# Revit family: HSS-Round Hollow Structural Section-Column
name_source: partatom
category: Structural Columns
revit_build: Autodesk Revit Architecture 2012 (Build: 20110210_1515)
units: mm (PartAtom-declared; Revit-internal decimal feet)

## types (153) — shared parameters
Assembly Code = B10

## per-type parameters (varying)
| type | A | OD | W | t |
| HSS20X0.500 | 28.5 in² | 1' - 8" | 104 | 0' - 0 15/32" |
| HSS20X0.375 | 21.5 in² | 1' - 8" | 78.7 | 0' - 0 11/32" |
| HSS18X0.500 | 25.6 in² | 1' - 6" | 93.5 | 0' - 0 15/32" |
| HSS18X0.375 | 19.4 in² | 1' - 6" | 70.7 | 0' - 0 11/32" |
| HSS16X0.625 | 28.1 in² | 1' - 4" | 103 | 0' - 0 19/32" |
| HSS16X0.500 | 22.7 in² | 1' - 4" | 82.8 | 0' - 0 15/32" |
| HSS16X0.438 | 19.9 in² | 1' - 4" | 72.9 | 0' - 0 13/32" |
| HSS16X0.375 | 17.2 in² | 1' - 4" | 62.6 | 0' - 0 11/32" |
| HSS16X0.312 | 14.4 in² | 1' - 4" | 52.3 | 0' - 0 9/32" |
| HSS16X0.250 | 11.5 in² | 1' - 4" | 42.1 | 0' - 0 7/32" |
| HSS14X0.625 | 24.5 in² | 1' - 2" | 89.4 | 0' - 0 19/32" |
| HSS14X0.500 | 19.8 in² | 1' - 2" | 72.2 | 0' - 0 15/32" |
| HSS14X0.375 | 15 in² | 1' - 2" | 54.6 | 0' - 0 11/32" |
| HSS14X0.312 | 12.5 in² | 1' - 2" | 45.7 | 0' - 0 9/32" |
| HSS14X0.250 | 10.1 in² | 1' - 2" | 36.7 | 0' - 0 7/32" |
| HSS12.750X0.500 | 17.9 in² | 1' - 0 3/4" | 65.5 | 0' - 0 15/32" |
| HSS12.750X0.375 | 13.6 in² | 1' - 0 3/4" | 49.6 | 0' - 0 11/32" |
| HSS12.750X0.250 | 9.16 in² | 1' - 0 3/4" | 33.4 | 0' - 0 7/32" |
| HSS12.500X.625 - Obsolete | 21.8 in² | 1' - 0 1/2" | 79.3 | 0' - 0 19/32" |
| HSS12.500X.500 - Obsolete | 17.6 in² | 1' - 0 1/2" | 64.1 | 0' - 0 15/32" |
| HSS12.500X.375 - Obsolete | 13.3 in² | 1' - 0 1/2" | 48.6 | 0' - 0 11/32" |
| HSS12.500X.312 - Obsolete | 11.2 in² | 1' - 0 1/2" | 40.7 | 0' - 0 9/32" |
| HSS12.500X.250 - Obsolete | 9 in² | 1' - 0 1/2" | 32.7 | 0' - 0 7/32" |
| HSS12.500X.188 - Obsolete | 6.7 in² | 1' - 0 1/2" | 24.7 | 0' - 0 3/16" |
| HSS11.250X.625 - Obsolete | 19.5 in² | 0' - 11 1/4" | 71 | 0' - 0 19/32" |
| HSS11.250X.500 - Obsolete | 15.8 in² | 0' - 11 1/4" | 57.5 | 0' - 0 15/32" |
| HSS11.250X.375 - Obsolete | 12 in² | 0' - 11 1/4" | 43.6 | 0' - 0 11/32" |
| HSS11.250X.312 - Obsolete | 10 in² | 0' - 11 1/4" | 36.5 | 0' - 0 9/32" |
| HSS11.250X.250 - Obsolete | 8.1 in² | 0' - 11 1/4" | 29.4 | 0' - 0 7/32" |
| HSS11.250X.188 - Obsolete | 6.1 in² | 0' - 11 1/4" | 22.2 | 0' - 0 3/16" |
| HSS10.750X0.500 | 15 in² | 0' - 10 3/4" | 54.8 | 0' - 0 15/32" |
| HSS10.750X0.375 | 11.4 in² | 0' - 10 3/4" | 41.6 | 0' - 0 11/32" |
| HSS10.750X0.250 | 7.7 in² | 0' - 10 3/4" | 28.1 | 0' - 0 7/32" |
| HSS10X0.625 | 17.2 in² | 0' - 10" | 62.6 | 0' - 0 19/32" |
| HSS10X0.500 | 13.9 in² | 0' - 10" | 50.8 | 0' - 0 15/32" |
| HSS10X0.375 | 10.6 in² | 0' - 10" | 38.6 | 0' - 0 11/32" |
| HSS10X0.312 | 8.88 in² | 0' - 10" | 32.3 | 0' - 0 9/32" |
| HSS10X0.250 | 7.15 in² | 0' - 10" | 26.1 | 0' - 0 7/32" |
| HSS10X0.188 | 5.37 in² | 0' - 10" | 19.7 | 0' - 0 3/16" |
| HSS9.625X0.500 | 13.4 in² | 0' - 9 5/8" | 48.8 | 0' - 0 15/32" |
| HSS9.625X0.375 | 10.2 in² | 0' - 9 5/8" | 37.1 | 0' - 0 11/32" |
| HSS9.625X0.312 | 8.53 in² | 0' - 9 5/8" | 31.1 | 0' - 0 9/32" |
| HSS9.625X0.250 | 6.87 in² | 0' - 9 5/8" | 25.1 | 0' - 0 7/32" |
| HSS9.625X0.188 | 5.17 in² | 0' - 9 5/8" | 19 | 0' - 0 3/16" |
| HSS8.750X.500 - Obsolete | 12.1 in² | 0' - 8 3/4" | 44.1 | 0' - 0 15/32" |
| HSS8.750X.375 - Obsolete | 9.2 in² | 0' - 8 3/4" | 33.6 | 0' - 0 11/32" |
| HSS8.750X.312 - Obsolete | 7.7 in² | 0' - 8 3/4" | 28.1 | 0' - 0 9/32" |
| HSS8.750X.250 - Obsolete | 6.2 in² | 0' - 8 3/4" | 22.7 | 0' - 0 7/32" |
| HSS8.750X.188 - Obsolete | 4.7 in² | 0' - 8 3/4" | 17.2 | 0' - 0 3/16" |
| HSS8.625X0.625 | 14.7 in² | 0' - 8 5/8" | 53.5 | 0' - 0 19/32" |
| HSS8.625X0.500 | 11.9 in² | 0' - 8 5/8" | 43.4 | 0' - 0 15/32" |
| HSS8.625X0.375 | 9.07 in² | 0' - 8 5/8" | 33.1 | 0' - 0 11/32" |
| HSS8.625X0.322 | 7.85 in² | 0' - 8 5/8" | 28.6 | 0' - 0 5/16" |
| HSS8.625X0.250 | 6.14 in² | 0' - 8 5/8" | 22.4 | 0' - 0 7/32" |
| HSS8.625X0.188 | 4.62 in² | 0' - 8 5/8" | 17 | 0' - 0 3/16" |
| HSS7.625X0.375 | 7.98 in² | 0' - 8 5/8" | 29.1 | 0' - 0 11/32" |
| HSS7.625X0.328 | 7.01 in² | 0' - 8 5/8" | 25.6 | 0' - 0 5/16" |
| HSS7.625X0.125 - Obsolete | 2.7 in² | 0' - 7 5/8" | 10 | 0' - 0 1/8" |
| HSS7.500X0.500 | 10.3 in² | 0' - 7 1/2" | 37.4 | 0' - 0 15/32" |
| HSS7.500X0.375 | 7.84 in² | 0' - 7 1/2" | 28.6 | 0' - 0 11/32" |
| HSS7.500X0.312 | 6.59 in² | 0' - 7 1/2" | 24 | 0' - 0 9/32" |
| HSS7.500X0.250 | 5.32 in² | 0' - 7 1/2" | 19.4 | 0' - 0 7/32" |
| HSS7.500X0.188 | 4 in² | 0' - 7 1/2" | 14.7 | 0' - 0 3/16" |
| HSS7X0.500 | 9.55 in² | 0' - 7" | 34.7 | 0' - 0 15/32" |
| HSS7X0.375 | 7.29 in² | 0' - 7" | 26.6 | 0' - 0 11/32" |
| HSS7X0.312 | 6.13 in² | 0' - 7" | 22.3 | 0' - 0 9/32" |
| HSS7X0.250 | 4.95 in² | 0' - 7" | 18 | 0' - 0 7/32" |
| HSS7X0.188 | 3.73 in² | 0' - 7" | 13.7 | 0' - 0 3/16" |
| HSS7X0.125 | 2.51 in² | 0' - 7" | 9.19 | 0' - 0 1/8" |
| HSS6.875X0.500 | 9.36 in² | 0' - 6 7/8" | 34.1 | 0' - 0 15/32" |
| HSS6.875X0.375 | 7.16 in² | 0' - 6 7/8" | 26.1 | 0' - 0 11/32" |
| HSS6.875X0.312 | 6.02 in² | 0' - 6 7/8" | 21.9 | 0' - 0 9/32" |
| HSS6.875X0.250 | 4.86 in² | 0' - 6 7/8" | 17.7 | 0' - 0 7/32" |
| HSS6.875X0.188 | 3.66 in² | 0' - 6 7/8" | 13.4 | 0' - 0 3/16" |
| HSS6.625X0.500 | 9 in² | 0' - 6 5/8" | 32.7 | 0' - 0 15/32" |
| HSS6.625X0.432 | 7.86 in² | 0' - 6 5/8" | 28.6 | 0' - 0 13/32" |
| HSS6.625X0.375 | 6.88 in² | 0' - 6 5/8" | 25.1 | 0' - 0 11/32" |
| HSS6.625X0.312 | 5.79 in² | 0' - 6 5/8" | 21.1 | 0' - 0 9/32" |
| HSS6.625X0.280 | 5.2 in² | 0' - 6 5/8" | 19 | 0' - 0 1/4" |
| HSS6.625X0.250 | 4.68 in² | 0' - 6 5/8" | 17 | 0' - 0 7/32" |
| HSS6.625X0.188 | 3.53 in² | 0' - 6 5/8" | 12.9 | 0' - 0 3/16" |
| HSS6.625X0.125 | 2.37 in² | 0' - 6 5/8" | 8.69 | 0' - 0 1/8" |
| HSS6.125X0.500 - Obsolete | 8.3 in² | 0' - 6 1/8" | 30.1 | 0' - 0 15/32" |
| HSS6.125X0.375 - Obsolete | 6.3 in² | 0' - 6 1/8" | 23.1 | 0' - 0 11/32" |
| HSS6.125X0.312 - Obsolete | 5.3 in² | 0' - 6 1/8" | 19.4 | 0' - 0 9/32" |
| HSS6.125X0.250 - Obsolete | 4.3 in² | 0' - 6 1/8" | 15.7 | 0' - 0 7/32" |
| HSS6.125X0.188 - Obsolete | 3.3 in² | 0' - 6 1/8" | 11.9 | 0' - 0 3/16" |
| HSS6X0.500 | 8.09 in² | 0' - 6" | 29.4 | 0' - 0 15/32" |
| HSS6X0.375 | 6.2 in² | 0' - 6" | 22.5 | 0' - 0 11/32" |
| HSS6X0.312 | 5.22 in² | 0' - 6" | 19 | 0' - 0 9/32" |
| HSS6X0.280 | 4.69 in² | 0' - 6" | 17.1 | 0' - 0 1/4" |
| HSS6X0.250 | 4.22 in² | 0' - 6" | 15.4 | 0' - 0 7/32" |
| HSS6X0.188 | 3.18 in² | 0' - 6" | 11.7 | 0' - 0 3/16" |
| HSS6X0.125 | 2.14 in² | 0' - 6" | 7.85 | 0' - 0 1/8" |
| HSS5.563X0.500 | 7.45 in² | 0' - 5 9/16" | 27.1 | 0' - 0 15/32" |
| HSS5.563X0.375 | 5.72 in² | 0' - 5 9/16" | 20.8 | 0' - 0 11/32" |
| HSS5.563X0.258 | 4.01 in² | 0' - 5 9/16" | 14.6 | 0' - 0 1/4" |
| HSS5.563X0.188 | 2.95 in² | 0' - 5 9/16" | 10.8 | 0' - 0 3/16" |
| HSS5.563X0.134 | 2.12 in² | 0' - 5 9/16" | 7.78 | 0' - 0 1/8" |
| HSS5.500X0.500 | 7.36 in² | 0' - 5 1/2" | 26.7 | 0' - 0 15/32" |
| HSS5.500X0.375 | 5.65 in² | 0' - 5 1/2" | 20.5 | 0' - 0 11/32" |
| HSS5.500X0.258 | 3.97 in² | 0' - 5 1/2" | 14.5 | 0' - 0 1/4" |
| HSS5X0.500 | 6.62 in² | 0' - 5" | 24.1 | 0' - 0 15/32" |
| HSS5X0.375 | 5.1 in² | 0' - 5" | 18.5 | 0' - 0 11/32" |
| HSS5X0.312 | 4.3 in² | 0' - 5" | 15.6 | 0' - 0 9/32" |
| HSS5X0.258 | 3.59 in² | 0' - 5" | 13.1 | 0' - 0 1/4" |
| HSS5X0.250 | 3.49 in² | 0' - 5" | 12.7 | 0' - 0 7/32" |
| HSS5X0.188 | 2.64 in² | 0' - 5" | 9.67 | 0' - 0 3/16" |
| HSS5X0.125 | 1.78 in² | 0' - 5" | 6.51 | 0' - 0 1/8" |
| HSS4.500X0.375 | 4.55 in² | 0' - 4 1/2" | 16.5 | 0' - 0 11/32" |
| HSS4.500X0.337 | 4.12 in² | 0' - 4 1/2" | 15 | 0' - 0 5/16" |
| HSS4.500X0.237 | 2.96 in² | 0' - 4 1/2" | 10.8 | 0' - 0 7/32" |
| HSS4.500X0.188 | 2.36 in² | 0' - 4 1/2" | 8.67 | 0' - 0 3/16" |
| HSS4.500X0.125 | 1.6 in² | 0' - 4 1/2" | 5.85 | 0' - 0 1/8" |
| HSS4X0.337 - Obsolete | 3.7 in² | 0' - 4" | 13.2 | 0' - 0 5/16" |
| HSS4X0.313 | 3.39 in² | 0' - 4" | 12.3 | 0' - 0 9/32" |
| HSS4X0.250 | 2.76 in² | 0' - 4" | 10 | 0' - 0 7/32" |
| HSS4X0.237 | 2.61 in² | 0' - 4" | 9.53 | 0' - 0 7/32" |
| HSS4X0.226 | 2.5 in² | 0' - 4" | 9.12 | 0' - 0 7/32" |
| HSS4X0.220 | 2.44 in² | 0' - 4" | 8.89 | 0' - 0 7/32" |
| HSS4X0.188 | 2.09 in² | 0' - 4" | 7.66 | 0' - 0 3/16" |
| HSS4X0.125 | 1.42 in² | 0' - 4" | 5.18 | 0' - 0 1/8" |
| HSS3.500X0.313 | 2.93 in² | 0' - 3 1/2" | 10.7 | 0' - 0 9/32" |
| HSS3.500X0.300 | 2.82 in² | 0' - 3 1/2" | 10.3 | 0' - 0 9/32" |
| HSS3.500X0.250 | 2.39 in² | 0' - 3 1/2" | 8.69 | 0' - 0 7/32" |
| HSS3.500X0.216 | 2.08 in² | 0' - 3 1/2" | 7.58 | 0' - 0 3/16" |
| HSS3.500X0.203 | 1.97 in² | 0' - 3 1/2" | 7.15 | 0' - 0 3/16" |
| HSS3.500X0.188 | 1.82 in² | 0' - 3 1/2" | 6.66 | 0' - 0 3/16" |
| HSS3.500X0.125 | 1.23 in² | 0' - 3 1/2" | 4.51 | 0' - 0 1/8" |
| HSS3X0.300 - Obsolete | 2.4 in² | 0' - 3" | 8.7 | 0' - 0 9/32" |
| HSS3X0.250 | 2.03 in² | 0' - 3" | 7.35 | 0' - 0 7/32" |
| HSS3X0.216 | 1.77 in² | 0' - 3" | 6.43 | 0' - 0 3/16" |
| HSS3X0.203 | 1.67 in² | 0' - 3" | 6.07 | 0' - 0 3/16" |
| HSS3X0.188 | 1.54 in² | 0' - 3" | 5.65 | 0' - 0 3/16" |
| HSS3X0.152 | 1.27 in² | 0' - 3" | 4.63 | 0' - 0 5/32" |
| HSS3X0.134 | 1.12 in² | 0' - 3" | 4.11 | 0' - 0 1/8" |
| HSS3X0.125 | 1.05 in² | 0' - 3" | 3.84 | 0' - 0 1/8" |
| HSS2.875X0.250 | 1.93 in² | 0' - 2 7/8" | 7.02 | 0' - 0 7/32" |
| HSS2.875X0.203 | 1.59 in² | 0' - 2 7/8" | 5.8 | 0' - 0 3/16" |
| HSS2.875X0.188 | 1.48 in² | 0' - 2 7/8" | 5.4 | 0' - 0 3/16" |
| HSS2.875X0.125 | 1.01 in² | 0' - 2 7/8" | 3.67 | 0' - 0 1/8" |
| HSS2.500X0.250 | 1.66 in² | 0' - 2 1/2" | 6.01 | 0' - 0 7/32" |
| HSS2.500X0.188 | 1.27 in² | 0' - 2 1/2" | 4.65 | 0' - 0 3/16" |
| HSS2.500X0.125 | 0.87 in² | 0' - 2 1/2" | 3.17 | 0' - 0 1/8" |
| HSS2.375X0.250 | 1.57 in² | 0' - 2 3/8" | 5.68 | 0' - 0 7/32" |
| HSS2.375X0.218 | 1.39 in² | 0' - 2 3/8" | 5.03 | 0' - 0 3/16" |
| HSS2.375X0.188 | 1.2 in² | 0' - 2 3/8" | 4.4 | 0' - 0 3/16" |
| HSS2.375X0.154 | 1 in² | 0' - 2 3/8" | 3.66 | 0' - 0 5/32" |
| HSS2.375X0.125 | 0.82 in² | 0' - 2 3/8" | 3.01 | 0' - 0 1/8" |
| HSS1.900X0.188 | 0.94 in² | 0' - 1 29/32" | 3.44 | 0' - 0 3/16" |
| HSS1.900X0.145 | 0.75 in² | 0' - 1 29/32" | 2.72 | 0' - 0 1/8" |
| HSS1.900X0.120 | 0.62 in² | 0' - 1 29/32" | 2.28 | 0' - 0 1/8" |
| HSS1.660X0.140 | 0.63 in² | 0' - 1 21/32" | 2.27 | 0' - 0 1/8" |

## geometry (parser evidence)
native form markers: Sweep x1
no freeform markers — native parametric forms only
